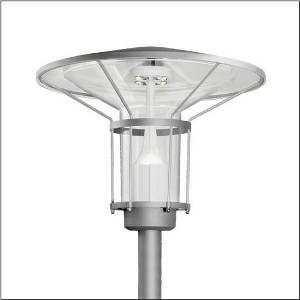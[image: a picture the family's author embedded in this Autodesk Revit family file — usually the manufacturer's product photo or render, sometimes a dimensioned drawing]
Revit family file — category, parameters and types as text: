
# Revit family: laterne_classic_iq___st1_2a_5xa5245mf14h_178e
name_source: partatom
category: Lighting Fixtures
units: mm (PartAtom-declared; Revit-internal decimal feet)

## family parameters
Cut with Voids When Loaded = No
Host = Face
Light Source = No
Part Type = Normal
Room Calculation Point = No
Round Connector Dimension = Use Diameter
Shared = No

## types (1)
- --- (1 x LED, 1380 lm, 11.8 W, 2700K)
    Apparent Load = 12 VA
    CIE Flux Codes = 21 60 93 97 100
    Color Rendering = 70
    Color Temperature = 2700K
    Default Elevation = 1800 mm
    Description = Lantern Classic iQ, mast luminaire, Module 540 iQ-SR, primary light control with 3 zone facetted reflector, of plastic, silver coated, highly specular, structured, primary optical cover: cover, of PMMA, transparent, light distribution: ST1.2a, light emission: direct distribution, primary light characteristic: asymmetric, installation type: post-top, LED, High Power LED, rated luminous flux: 1.380lm, luminous efficacy: 117lm/W, light colour: 727, colour temperature: 2700K, control gear: iQ Street-Remote, control: pre-setting: logarithmic dimming characteristic, Street-Remote, Auto-Match, Temp-Guard, Lumen-Switch, Night-Set, Smart-Wire, Light-Fading, Desk-Remote (wireless, voltage-free reading and setting of iQ features in the workshop via application-optimized NFC function/RFID function), optimised constant luminous flux control (CLO 2.0), with terminal, 6-pole, max. 2.5mm², mains connection: 230..240V, AC, 50/60Hz, start of lifetime: 12W, end of service life: 12W, reduction: 6W, luminaire housing, upper part, of glass-fibre reinforced polyester, coated, Siteco® metallic grey (DB 702S), diameter: 750mm, height: 596mm, spigot size: d x l = 76 x 70mm (post-top) | with reducer (optional accessory) 60 x 70mm, mounting height: 3..5m, post-top mast mounting element, of diecast aluminium, coated, Siteco® metallic grey (DB 702S), Module 540 iQ-SR, traffic white (RAL 9016), equipment: standard, protection rating (complete): IP65, insulation class (complete): insulation class II (safety insulation), certification: CE, ENEC, VDE, packaging unit: 1 piece

Light Distribution: ST1.2a
    Height = 596 mm
    Lamp = 1 x LED
    Lamp Light Flux = 1380 lm
    Lamp Power = 11.8 W
    Lamp count = 1
    Length = 750 mm
    Luminous efficacy = 117 lm/W
    Manufacturer = Siteco
    ModVariant = No
    Model = 5XA5245MF14H
    Number of Poles = 1
    OnlyDefault = Yes
    Power Factor = 1
    Product Name = Laterne Classic iQ | ST1.2a
    Product group = mast luminaire | pylon top
    ProductGroupID = 6100
    Protection Class = Protection class II
    Protection Degree = IP 65
    RLX_Detail_Level = 1
    RLX_Emergency_Light_Flux = 0 lm
    RLX_Emergency_Type = 0
    RLX_Emergency_Type_DB = No
    RlxData = <blob elided: 91757 chars, md5=b8e4b43f>
    Socket = socket
    Standby Power = 0 W
    System Light Flux = 1380 lm
    System Power = 12 W
    Type Comments = factory setting: luminous flux: 100 % | dim-lin: 254 | 472 mA
    Type Image = l_1006052.jpg
    URL = http://relux.com
    VarID = @adj_174823
    Voltage = 0 V
    Weight = 0.00 kg
    Width = 0 mm  [stored 0 ft]

note: [stored X ft] marks values corroborated as IEEE doubles in the binary element streams (Revit-internal decimal feet)

## geometry (parser evidence)
native form markers: Blend x4, Sweep x10
no freeform markers — native parametric forms only
